# Revit family: Sanitary_Showers_hansgrohe_26843CHN-Rainfinity-Wall-outlet-Porter-5_NEW
name_source: partatom
category: Plumbing Fixtures
revit_build: Autodesk Revit 2018 (Build: 20170223_1515(x64)
units: mm (PartAtom-declared; Revit-internal decimal feet)

## family parameters
Always vertical = No
Cut with Voids When Loaded = No
OmniClass Number = 23.31.17.00
OmniClass Title = Showers
Part Type = Normal
Room Calculation Point = No
Round Connector Dimension = Use Diameter
Shared = No
Work Plane-Based = Yes

## types (6) — shared parameters
Always visible = Yes
BIMobject category = Showers
Connector Description = Water Inlet 12.7mm
Default Elevation = 1219.2 mm  [stored 4 ft]
Description = Rainfinity Wall outlet Porter 500 with shower holder and shower shelf left
Diameter = 13 mm
Edition number = 1
IFC Classification = Sanitary Terminal
Manufacturer = Hansgrohe
Manufacturer name = hansgrohe
Model = 26843CHN
OmniClass Code = 23-31 17 00
OmniClass Description = Showers
Outlet Connector Description = Water Outlet 12.7mm
Outlet Diameter = 13 mm
Product Guid = 18def00e-5102-46cf-8268-ec18ad407bc2
Product SKU = 26843CHN
Product data url = https://bimobject.com
Product family = Rainfinity
Product group = Wall outlet
Product name = 26843CHN Rainfinity Wall outlet Porter 500 with shower holder and shower shelf left
Product url = https://www.hansgrohe.com
QR code = https://bimobject.com
URL = https://www.hansgrohe.com
Weight Net (Kg) = 2

## per-type parameters (varying)
| type | Material 1 | Material 2 |
| 997 Polished Gold Optic | Hansgrohe - Plastic - Graphite | Hansgrohe - Metal - 997 Polished Gold Optic |
| 707 Matt White | Hansgrohe - Plastic - Graphite | Hansgrohe - Metal - 707 Matt White |
| 677 Matt Black | Hansgrohe - Plastic - Graphite | Hansgrohe - Metal - 677 Matt Black |
| 347 Brushed Black Chrome | Hansgrohe - Plastic - Graphite | Hansgrohe - Metal - 347 Brushed Black Chrome |
| 147 Brushed Bronze | Hansgrohe - Plastic - Graphite | Hansgrohe - Metal - 147 Brushed Bronze |
| 007 Chrome | Hansgrohe - Glass - Mirror glass | Hansgrohe - Metal - 007 Chrome |

note: [stored X ft] marks values corroborated as IEEE doubles in the binary element streams (Revit-internal decimal feet)

## geometry (parser evidence)
native form markers: Sweep x2
no freeform markers — native parametric forms only
